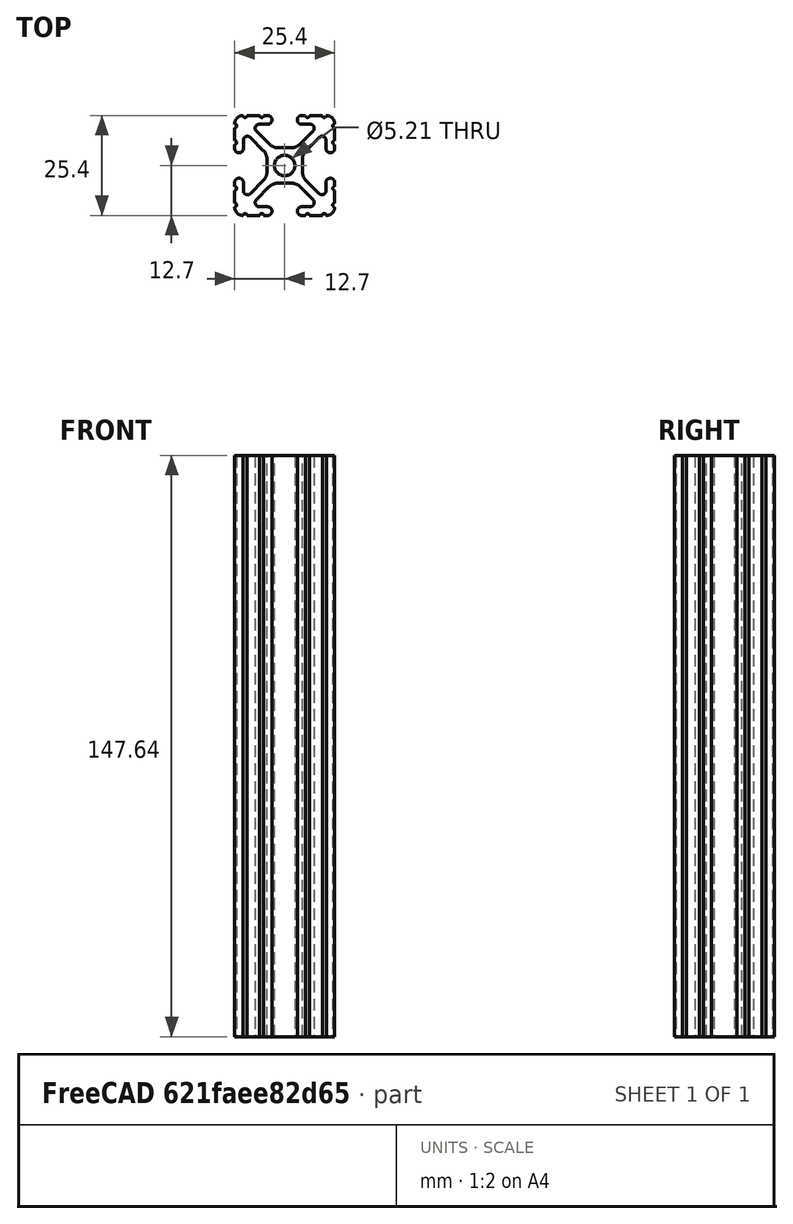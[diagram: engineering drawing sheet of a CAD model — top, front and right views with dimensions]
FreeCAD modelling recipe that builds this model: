
FCSTD DOCUMENT  (FreeCAD 0.19R23756 (Git))
Label: 1010-5p8125
License: All rights reserved
LicenseURL: http://en.wikipedia.org/wiki/All_rights_reserved
objects: Sketcher::SketchObject×1, Part::Extrusion×1
note: 2 computed .brp shape members not serialized (recipe doc carries the construction recipe); baked Part::Feature solids carry a one-line shape summary decoded from their .brp

FEATURE [Sketcher::SketchObject] Sketch097
  FullyConstrained = false
  sketch-geometry (97):
    g0: Circle CenterX=0 CenterY=0 CenterZ=0 NormalX=0 NormalY=0 NormalZ=-1 AngleXU=0 Radius=2.6035
    g1: ArcOfCircle CenterX=12.7 CenterY=5.82508 CenterZ=0 NormalX=0 NormalY=0 NormalZ=1 AngleXU=0 Radius=0.508 StartAngle=1.5708 EndAngle=4.71239
    g2: LineSegment StartX=3.2385 StartY=11.651 StartZ=0 EndX=3.2385 EndY=11.5392 EndZ=0
    g3: LineSegment StartX=6.33313 StartY=-12.7 StartZ=0 EndX=9.55044 EndY=-12.7 EndZ=0
    g4: LineSegment StartX=7.20704 StartY=8.72437 StartZ=0 EndX=3.89827 EndY=5.42317 EndZ=0
    g5: ArcOfCircle CenterX=7.6835 CenterY=1.59319 CenterZ=0 NormalX=0 NormalY=0 NormalZ=1 AngleXU=0 Radius=3.175 StartAngle=2.35505 EndAngle=3.14159
    g6: ArcOfCircle CenterX=-1.70925 CenterY=-7.6708 CenterZ=0 NormalX=0 NormalY=0 NormalZ=1 AngleXU=0 Radius=3.175 StartAngle=1.5708 EndAngle=2.35528
    g7: ArcOfCircle CenterX=11.5392 CenterY=-4.28747 CenterZ=0 NormalX=0 NormalY=0 NormalZ=1 AngleXU=0 Radius=1.04901 StartAngle=1.5708 EndAngle=3.14159
    g8: ArcOfCircle CenterX=12.7 CenterY=-5.82508 CenterZ=0 NormalX=0 NormalY=0 NormalZ=1 AngleXU=0 Radius=0.508 StartAngle=1.5708 EndAngle=4.71239
    g9: LineSegment StartX=4.28751 StartY=10.4902 StartZ=0 EndX=6.47679 EndY=10.4902 EndZ=0
    g10: ArcOfCircle CenterX=4.28751 CenterY=11.651 CenterZ=0 NormalX=0 NormalY=0 NormalZ=1 AngleXU=0 Radius=1.04901 StartAngle=1.5708 EndAngle=3.14159
    g11: ArcOfCircle CenterX=6.47679 CenterY=9.45629 CenterZ=0 NormalX=0 NormalY=0 NormalZ=1 AngleXU=0 Radius=1.03391 StartAngle=5.49664 EndAngle=7.85398
    g12: ArcOfCircle CenterX=4.28751 CenterY=11.5392 CenterZ=0 NormalX=0 NormalY=0 NormalZ=1 AngleXU=0 Radius=1.04901 StartAngle=3.14159 EndAngle=4.71239
    g13: LineSegment StartX=3.95227 StartY=-5.42369 StartZ=0 EndX=7.17965 EndY=-8.64519 EndZ=0
    g14: ArcOfCircle CenterX=11.651 CenterY=4.28747 CenterZ=0 NormalX=0 NormalY=0 NormalZ=1 AngleXU=0 Radius=1.04901 StartAngle=4.71239 EndAngle=6.28319
    g15: ArcOfCircle CenterX=-5.82513 CenterY=-12.7 CenterZ=0 NormalX=0 NormalY=0 NormalZ=1 AngleXU=0 Radius=0.508 StartAngle=0 EndAngle=3.14159
    g16: LineSegment StartX=-6.47679 StartY=10.4902 StartZ=0 EndX=-4.28751 EndY=10.4902 EndZ=0
    g17: ArcOfCircle CenterX=-12.7 CenterY=10.0584 CenterZ=0 NormalX=0 NormalY=0 NormalZ=1 AngleXU=0 Radius=0.508 StartAngle=4.71239 EndAngle=7.85368
    g18: ArcOfCircle CenterX=-12.7 CenterY=5.82508 CenterZ=0 NormalX=0 NormalY=0 NormalZ=1 AngleXU=0 Radius=0.508 StartAngle=4.71239 EndAngle=7.85398
    g19: LineSegment StartX=-11.5392 StartY=-3.23846 StartZ=0 EndX=-11.651 EndY=-3.23846 EndZ=0
    g20: LineSegment StartX=-3.89827 StartY=5.42317 StartZ=0 EndX=-7.20704 EndY=8.72437 EndZ=0
    g21: LineSegment StartX=1.65578 StartY=4.4958 StartZ=0 EndX=-1.65578 EndY=4.4958 EndZ=0
    g22: ArcOfCircle CenterX=-1.65578 CenterY=7.6708 CenterZ=0 NormalX=0 NormalY=0 NormalZ=1 AngleXU=0 Radius=3.175 StartAngle=3.92813 EndAngle=4.71239
    g23: LineSegment StartX=-9.55044 StartY=-12.7 StartZ=0 EndX=-6.33313 EndY=-12.7 EndZ=0
    g24: ArcOfCircle CenterX=-5.82513 CenterY=12.7 CenterZ=0 NormalX=0 NormalY=0 NormalZ=1 AngleXU=0 Radius=0.508 StartAngle=3.14159 EndAngle=6.28319
    g25: ArcOfCircle CenterX=-4.28751 CenterY=11.651 CenterZ=0 NormalX=0 NormalY=0 NormalZ=1 AngleXU=0 Radius=1.04901 StartAngle=0 EndAngle=1.5708
    g26: LineSegment StartX=-12.7 StartY=-4.28747 StartZ=0 EndX=-12.7 EndY=-5.31708 EndZ=0
    g27: ArcOfCircle CenterX=-6.47679 CenterY=9.45629 CenterZ=0 NormalX=0 NormalY=0 NormalZ=1 AngleXU=0 Radius=1.03391 StartAngle=1.5708 EndAngle=3.92813
    g28: ArcOfCircle CenterX=-4.28751 CenterY=11.5392 CenterZ=0 NormalX=0 NormalY=0 NormalZ=1 AngleXU=0 Radius=1.04901 StartAngle=4.71239 EndAngle=6.28319
    g29: LineSegment StartX=-5.44101 StartY=-3.84082 StartZ=0 EndX=-8.73713 EndY=-7.12941 EndZ=0
    g30: ArcOfCircle CenterX=-7.6835 CenterY=-1.59319 CenterZ=0 NormalX=0 NormalY=0 NormalZ=1 AngleXU=0 Radius=3.175 StartAngle=5.49664 EndAngle=6.28319
    g31: LineSegment StartX=-12.7 StartY=5.31708 StartZ=0 EndX=-12.7 EndY=4.28747 EndZ=0
    g32: LineSegment StartX=-8.73713 StartY=7.12941 StartZ=0 EndX=-5.44101 EndY=3.84082 EndZ=0
    g33: LineSegment StartX=-11.651 StartY=3.23846 StartZ=0 EndX=-11.5392 EndY=3.23846 EndZ=0
    g34: ArcOfCircle CenterX=-9.46279 CenterY=-6.40209 CenterZ=0 NormalX=0 NormalY=0 NormalZ=1 AngleXU=0 Radius=1.02741 StartAngle=3.14159 EndAngle=5.49664
    g35: ArcOfCircle CenterX=-10.5918 CenterY=10.5918 CenterZ=0 NormalX=0 NormalY=0 NormalZ=1 AngleXU=0 Radius=2.1082 StartAngle=1.55877 EndAngle=3.15364
    g36: LineSegment StartX=-12.7 StartY=9.5504 StartZ=0 EndX=-12.7 EndY=6.33308 EndZ=0
    g37: LineSegment StartX=-6.33313 StartY=12.7 StartZ=0 EndX=-9.55044 EndY=12.7 EndZ=0
    g38: ArcOfCircle CenterX=-11.5392 CenterY=-4.28747 CenterZ=0 NormalX=0 NormalY=0 NormalZ=1 AngleXU=0 Radius=1.04901 StartAngle=0 EndAngle=1.5708
    g39: LineSegment StartX=4.28751 StartY=-12.7 StartZ=0 EndX=5.31713 EndY=-12.7 EndZ=0
    g40: LineSegment StartX=5.44101 StartY=3.84082 StartZ=0 EndX=8.73713 EndY=7.12941 EndZ=0
    g41: LineSegment StartX=10.4902 StartY=-4.28747 StartZ=0 EndX=10.4902 EndY=-6.40209 EndZ=0
    g42: ArcOfCircle CenterX=9.46279 CenterY=6.40209 CenterZ=0 NormalX=0 NormalY=0 NormalZ=1 AngleXU=0 Radius=1.02741 StartAngle=0 EndAngle=2.35505
    g43: ArcOfCircle CenterX=5.82513 CenterY=-12.7 CenterZ=0 NormalX=0 NormalY=0 NormalZ=1 AngleXU=0 Radius=0.508 StartAngle=0 EndAngle=3.14159
    g44: LineSegment StartX=12.7 StartY=-9.5504 StartZ=0 EndX=12.7 EndY=-6.33308 EndZ=0
    g45: LineSegment StartX=4.5085 StartY=-1.59319 StartZ=0 EndX=4.5085 EndY=1.59319 EndZ=0
    g46: ArcOfCircle CenterX=12.7 CenterY=10.0584 CenterZ=0 NormalX=0 NormalY=0 NormalZ=1 AngleXU=0 Radius=0.508 StartAngle=1.5711 EndAngle=4.71239
    g47: ArcOfCircle CenterX=12.7 CenterY=-10.0584 CenterZ=0 NormalX=0 NormalY=0 NormalZ=1 AngleXU=0 Radius=0.508 StartAngle=1.5708 EndAngle=4.71209
    g48: LineSegment StartX=3.2385 StartY=-11.5392 StartZ=0 EndX=3.2385 EndY=-11.651 EndZ=0
    g49: LineSegment StartX=8.73713 StartY=-7.12941 StartZ=0 EndX=5.44101 EndY=-3.84082 EndZ=0
    g50: ArcOfCircle CenterX=11.651 CenterY=-4.28747 CenterZ=0 NormalX=0 NormalY=0 NormalZ=1 AngleXU=0 Radius=1.04901 StartAngle=0 EndAngle=1.5708
    g51: ArcOfCircle CenterX=1.65578 CenterY=7.6708 CenterZ=0 NormalX=0 NormalY=0 NormalZ=1 AngleXU=0 Radius=3.175 StartAngle=4.71239 EndAngle=5.49664
    g52: ArcOfCircle CenterX=7.6835 CenterY=-1.59319 CenterZ=0 NormalX=0 NormalY=0 NormalZ=1 AngleXU=0 Radius=3.175 StartAngle=3.14159 EndAngle=3.92813
    g53: LineSegment StartX=12.7 StartY=4.28747 StartZ=0 EndX=12.7 EndY=5.31708 EndZ=0
    g54: ArcOfCircle CenterX=6.41641 CenterY=-9.40983 CenterZ=0 NormalX=0 NormalY=0 NormalZ=1 AngleXU=0 Radius=1.08037 StartAngle=4.71239 EndAngle=7.06949
    g55: LineSegment StartX=12.7 StartY=-5.31708 StartZ=0 EndX=12.7 EndY=-4.28747 EndZ=0
    g56: ArcOfCircle CenterX=10.0584 CenterY=-12.7 CenterZ=0 NormalX=0 NormalY=0 NormalZ=1 AngleXU=0 Radius=0.508 StartAngle=0.000300194 EndAngle=3.14159
    g57: ArcOfCircle CenterX=11.5392 CenterY=4.28747 CenterZ=0 NormalX=0 NormalY=0 NormalZ=1 AngleXU=0 Radius=1.04901 StartAngle=3.14159 EndAngle=4.71239
    g58: LineSegment StartX=12.7 StartY=6.33308 StartZ=0 EndX=12.7 EndY=9.5504 EndZ=0
    g59: ArcOfCircle CenterX=4.28751 CenterY=-11.5392 CenterZ=0 NormalX=0 NormalY=0 NormalZ=1 AngleXU=0 Radius=1.04901 StartAngle=1.5708 EndAngle=3.14159
    g60: ArcOfCircle CenterX=10.5918 CenterY=10.5918 CenterZ=0 NormalX=0 NormalY=0 NormalZ=1 AngleXU=0 Radius=2.1082 StartAngle=6.27114 EndAngle=7.86601
    g61: ArcOfCircle CenterX=9.46279 CenterY=-6.40209 CenterZ=0 NormalX=0 NormalY=0 NormalZ=1 AngleXU=0 Radius=1.02741 StartAngle=3.92813 EndAngle=6.28319
    g62: LineSegment StartX=6.41641 StartY=-10.4902 StartZ=0 EndX=4.28751 EndY=-10.4902 EndZ=0
    g63: LineSegment StartX=-10.4902 StartY=-6.40209 StartZ=0 EndX=-10.4902 EndY=-4.28747 EndZ=0
    g64: ArcOfCircle CenterX=-9.46279 CenterY=6.40209 CenterZ=0 NormalX=0 NormalY=0 NormalZ=1 AngleXU=0 Radius=1.02741 StartAngle=0.786542 EndAngle=3.14159
    g65: LineSegment StartX=-10.4902 StartY=4.28747 StartZ=0 EndX=-10.4902 EndY=6.40209 EndZ=0
    g66: LineSegment StartX=-4.5085 StartY=1.59319 StartZ=0 EndX=-4.5085 EndY=-1.59319 EndZ=0
    g67: LineSegment StartX=-4.28751 StartY=12.7 StartZ=0 EndX=-5.31713 EndY=12.7 EndZ=0
    g68: ArcOfCircle CenterX=-11.5392 CenterY=4.28747 CenterZ=0 NormalX=0 NormalY=0 NormalZ=1 AngleXU=0 Radius=1.04901 StartAngle=4.71239 EndAngle=6.28319
    g69: LineSegment StartX=-3.2385 StartY=11.5392 StartZ=0 EndX=-3.2385 EndY=11.651 EndZ=0
    g70: ArcOfCircle CenterX=-11.651 CenterY=4.28747 CenterZ=0 NormalX=0 NormalY=0 NormalZ=1 AngleXU=0 Radius=1.04901 StartAngle=3.14159 EndAngle=4.71239
    g71: ArcOfCircle CenterX=-7.6835 CenterY=1.59319 CenterZ=0 NormalX=0 NormalY=0 NormalZ=1 AngleXU=0 Radius=3.175 StartAngle=0 EndAngle=0.786542
    g72: ArcOfCircle CenterX=-10.0584 CenterY=12.7 CenterZ=0 NormalX=0 NormalY=0 NormalZ=1 AngleXU=0 Radius=0.508 StartAngle=3.14189 EndAngle=6.28319
    g73: LineSegment StartX=-1.70925 StartY=-4.4958 StartZ=0 EndX=1.70925 EndY=-4.4958 EndZ=0
    g74: LineSegment StartX=11.651 StartY=-3.23846 StartZ=0 EndX=11.5392 EndY=-3.23846 EndZ=0
    g75: ArcOfCircle CenterX=-10.5918 CenterY=-10.5918 CenterZ=0 NormalX=0 NormalY=0 NormalZ=1 AngleXU=0 Radius=2.1082 StartAngle=3.12954 EndAngle=4.72442
    g76: ArcOfCircle CenterX=10.5918 CenterY=-10.5918 CenterZ=0 NormalX=0 NormalY=0 NormalZ=1 AngleXU=0 Radius=2.1082 StartAngle=4.70036 EndAngle=6.29523
    g77: ArcOfCircle CenterX=-12.7 CenterY=-5.82508 CenterZ=0 NormalX=0 NormalY=0 NormalZ=1 AngleXU=0 Radius=0.508 StartAngle=4.71239 EndAngle=7.85398
    g78: ArcOfCircle CenterX=5.82513 CenterY=12.7 CenterZ=0 NormalX=0 NormalY=0 NormalZ=1 AngleXU=0 Radius=0.508 StartAngle=3.14159 EndAngle=6.28319
    g79: LineSegment StartX=9.55044 StartY=12.7 StartZ=0 EndX=6.33313 EndY=12.7 EndZ=0
    g80: ArcOfCircle CenterX=10.0584 CenterY=12.7 CenterZ=0 NormalX=0 NormalY=0 NormalZ=1 AngleXU=0 Radius=0.508 StartAngle=3.14159 EndAngle=6.28289
    g81: ArcOfCircle CenterX=1.70925 CenterY=-7.6708 CenterZ=0 NormalX=0 NormalY=0 NormalZ=1 AngleXU=0 Radius=3.175 StartAngle=0.78631 EndAngle=1.5708
    g82: ArcOfCircle CenterX=4.28751 CenterY=-11.651 CenterZ=0 NormalX=0 NormalY=0 NormalZ=1 AngleXU=0 Radius=1.04901 StartAngle=3.14159 EndAngle=4.71239
    g83: LineSegment StartX=5.31713 StartY=12.7 StartZ=0 EndX=4.28751 EndY=12.7 EndZ=0
    g84: LineSegment StartX=10.4902 StartY=6.40209 StartZ=0 EndX=10.4902 EndY=4.28747 EndZ=0
    g85: LineSegment StartX=11.5392 StartY=3.23846 StartZ=0 EndX=11.651 EndY=3.23846 EndZ=0
    g86: ArcOfCircle CenterX=-10.0584 CenterY=-12.7 CenterZ=0 NormalX=0 NormalY=0 NormalZ=1 AngleXU=0 Radius=0.508 StartAngle=0 EndAngle=3.14129
    g87: ArcOfCircle CenterX=-12.7 CenterY=-10.0584 CenterZ=0 NormalX=0 NormalY=0 NormalZ=1 AngleXU=0 Radius=0.508 StartAngle=4.71269 EndAngle=7.85398
    g88: ArcOfCircle CenterX=-4.28751 CenterY=-11.5392 CenterZ=0 NormalX=0 NormalY=0 NormalZ=1 AngleXU=0 Radius=1.04901 StartAngle=0 EndAngle=1.5708
    g89: ArcOfCircle CenterX=-4.28751 CenterY=-11.651 CenterZ=0 NormalX=0 NormalY=0 NormalZ=1 AngleXU=0 Radius=1.04901 StartAngle=4.71239 EndAngle=6.28319
    g90: LineSegment StartX=-12.7 StartY=-6.33308 StartZ=0 EndX=-12.7 EndY=-9.5504 EndZ=0
    g91: ArcOfCircle CenterX=-11.651 CenterY=-4.28747 CenterZ=0 NormalX=0 NormalY=0 NormalZ=1 AngleXU=0 Radius=1.04901 StartAngle=1.5708 EndAngle=3.14159
    g92: LineSegment StartX=-7.17965 StartY=-8.64519 StartZ=0 EndX=-3.95227 EndY=-5.42369 EndZ=0
    g93: LineSegment StartX=-5.31713 StartY=-12.7 StartZ=0 EndX=-4.28751 EndY=-12.7 EndZ=0
    g94: LineSegment StartX=-3.2385 StartY=-11.651 StartZ=0 EndX=-3.2385 EndY=-11.5392 EndZ=0
    g95: ArcOfCircle CenterX=-6.41641 CenterY=-9.40983 CenterZ=0 NormalX=0 NormalY=0 NormalZ=1 AngleXU=0 Radius=1.08037 StartAngle=2.35528 EndAngle=4.71239
    g96: LineSegment StartX=-4.28751 StartY=-10.4902 StartZ=0 EndX=-6.41641 EndY=-10.4902 EndZ=0
FEATURE [Part::Extrusion] Extrude
  Base = -> Sketch097
  Dir = (0,0,1)
  DirMode = 2
  FaceMakerClass = Part::FaceMakerBullseye
  LengthFwd = 147.637
  LengthRev = 0
  Solid = true
  Symmetric = false
